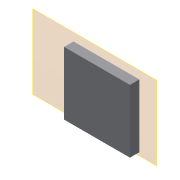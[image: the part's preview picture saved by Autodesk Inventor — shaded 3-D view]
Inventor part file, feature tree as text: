
AUTODESK INVENTOR PART (.ipt)
format: ipt  version: 2022 (Build 260153000, 153)  size: 107,520 bytes
history: native  units: in
note: dims shown in document units (in); Inventor stores cm internally (conversion verified against a paired STEP export)
features: other x3, extrude x2, sketch x2, plane x1, reference x1, projected_geometry x1
ambient origin geometry x8: Origin, YZ Plane, XZ Plane, XY Plane, X Axis, Y Axis, Z Axis, Center Point
bodies: Volumenkörper1 (feature_tree)
feature tree (10):
  plane  "Arbeitsebene1"
  extrude  "Extrusion1"  Depth=1.378in
  extrude  "Extrusion2"  Depth=0.0394in
  sketch  "Skizze1"  dims[d0=1.378in d1=1.378in]
  reference  "Referenz1"
  sketch  "Skizze2"  dims[d2=0.1929in d3=0.1929in d4=0.1929in d5=0.1575in d6=0.0in d7=0.0394in d8=0.0in]
  projected_geometry  "Projizierte Kontur1"
  other  "<userpath>\Documents\GitHub\cellstorm\INVENTOR\cellSTORM_v6.iam"
  other  "cellSTORM_v6.iam"
  other  "cellSTORM_v5_laserstage:1"
